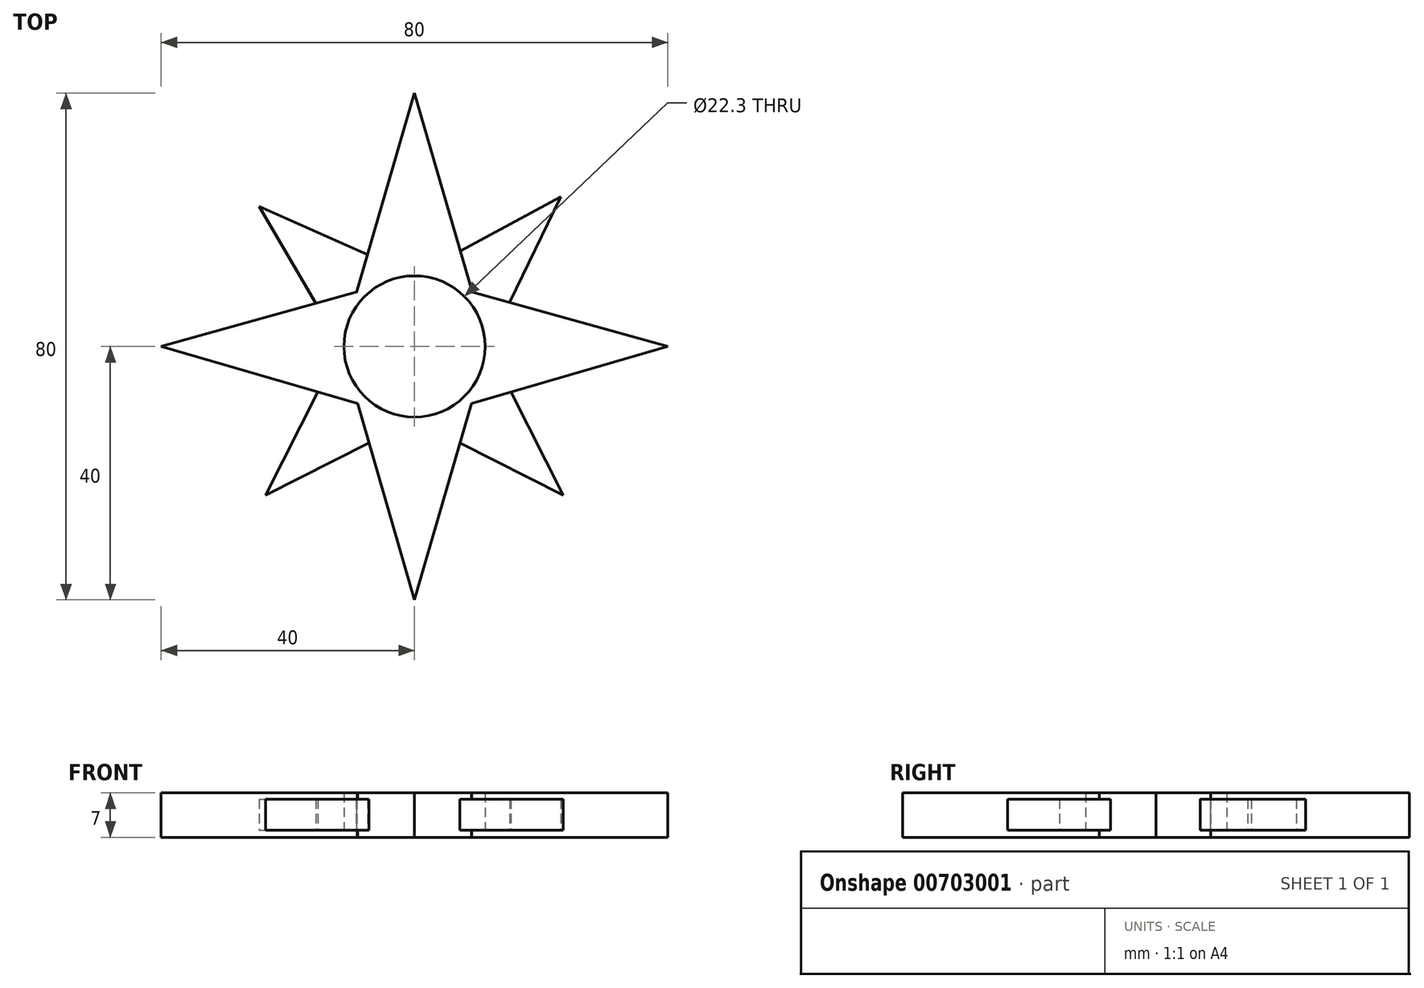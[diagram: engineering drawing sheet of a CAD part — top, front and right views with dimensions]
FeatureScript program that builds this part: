
annotation { "Feature Type Name" : "Feature", "Feature Type Description" : "" }
export const myFeature = defineFeature(function(context is Context, id is Id, definition is map)
    precondition{}
    {
        {
            var Q0;
            Q0=qCreatedBy(makeId("Top.planeOp"),FACE);
            var sketch = newSketch(context, id + "F0", { "sketchPlane" : qUnion([Q0])});
            skCircle(sketch, "E0", {"center": v(0, 0) * mm, "radius": 11.15 * mm});
            skLineSegment(sketch, "E1", {"start": v(0, 0) * mm, "end": v(0, 40) * mm});
            skLineSegment(sketch, "E2", {"start": v(0, 40) * mm, "end": v(-11.61, 0) * mm});
            skLineSegment(sketch, "E3", {"start": v(0, 40) * mm, "end": v(11.61, 0) * mm});
            skLineSegment(sketch, "E4", {"start": v(0, 0) * mm, "end": v(-40, 0) * mm});
            skLineSegment(sketch, "E5", {"start": v(0, 0) * mm, "end": v(0, -40) * mm});
            skLineSegment(sketch, "E6", {"start": v(0, 0) * mm, "end": v(40, 0) * mm});
            skLineSegment(sketch, "E7", {"start": v(0, 11.15) * mm, "end": v(-40, 0) * mm});
            skLineSegment(sketch, "E8", {"start": v(-40, 0) * mm, "end": v(0, -11.61) * mm});
            skLineSegment(sketch, "E9", {"start": v(0, -40) * mm, "end": v(-11.61, 0) * mm});
            skLineSegment(sketch, "E10", {"start": v(0, -40) * mm, "end": v(11.61, 0) * mm});
            skLineSegment(sketch, "E11", {"start": v(0, -11.61) * mm, "end": v(40, 0) * mm});
            skLineSegment(sketch, "E12", {"start": v(-11.61, 0) * mm, "end": v(0, 11.15) * mm});
            skLineSegment(sketch, "E13", {"start": v(0, 11.15) * mm, "end": v(40, 0) * mm});
            skLineSegment(sketch, "E14", {"start": v(-11.61, 0) * mm, "end": v(0, -11.61) * mm});
            skLineSegment(sketch, "E15", {"start": v(0, -11.61) * mm, "end": v(11.61, 0) * mm});
            skLineSegment(sketch, "E16", {"start": v(11.61, 0) * mm, "end": v(0, 11.15) * mm});
            skLineSegment(sketch, "E17", {"start": v(-5.8, 5.57) * mm, "end": v(-24.54, 22.13) * mm});
            skLineSegment(sketch, "E18", {"start": v(5.8, 5.58) * mm, "end": v(23.12, 23.6) * mm});
            skLineSegment(sketch, "E19", {"start": v(5.8, -5.8) * mm, "end": v(23.48, -23.48) * mm});
            skLineSegment(sketch, "E20", {"start": v(-5.8, -5.8) * mm, "end": v(-23.48, -23.48) * mm});
            skLineSegment(sketch, "E21", {"start": v(-24.54, 22.13) * mm, "end": v(-11.61, 0) * mm});
            skLineSegment(sketch, "E22", {"start": v(-24.54, 22.13) * mm, "end": v(0, 11.15) * mm});
            skLineSegment(sketch, "E23", {"start": v(0, 11.15) * mm, "end": v(23.12, 23.6) * mm});
            skLineSegment(sketch, "E24", {"start": v(23.12, 23.6) * mm, "end": v(11.61, 0) * mm});
            skLineSegment(sketch, "E25", {"start": v(11.61, 0) * mm, "end": v(23.48, -23.48) * mm});
            skLineSegment(sketch, "E26", {"start": v(23.48, -23.48) * mm, "end": v(0, -11.61) * mm});
            skLineSegment(sketch, "E27", {"start": v(0, -11.61) * mm, "end": v(-23.48, -23.48) * mm});
            skLineSegment(sketch, "E28", {"start": v(-23.48, -23.48) * mm, "end": v(-11.61, 0) * mm});
            skSolve(sketch);
        }
        {
            var Q0;
            {var subQ0=sQuery(id+"F0.wireOp",EDGE,"E2");var subQ3=sQuery(id+"F0.wireOp",EDGE,"E22");var subQ5=makeQuery(id+"F0.imprint","INTERSECT",VERTEX,{"derivedFrom":[subQ0,subQ3]});Q0=makeQuery(id+"F0.imprint","IMPRINT",FACE,{"disambiguationData":[TD([[makeQuery(id+"F0.imprint","IMPRINT",EDGE,{"disambiguationData":[TD([[subQ5,1.0]])],"derivedFrom":subQ0}),1.0]])]});}
            var Q1;
            {var subQ0=sQuery(id+"F0.wireOp",EDGE,"E3");var subQ3=sQuery(id+"F0.wireOp",EDGE,"E23");var subQ5=makeQuery(id+"F0.imprint","INTERSECT",VERTEX,{"derivedFrom":[subQ0,subQ3]});Q1=makeQuery(id+"F0.imprint","IMPRINT",FACE,{"disambiguationData":[TD([[makeQuery(id+"F0.imprint","IMPRINT",EDGE,{"disambiguationData":[TD([[subQ5,1.0]])],"derivedFrom":subQ0}),-1.0]])]});}
            var Q2;
            {var subQ0=sQuery(id+"F0.wireOp",EDGE,"E21");var subQ3=sQuery(id+"F0.wireOp",EDGE,"E7");var subQ5=makeQuery(id+"F0.imprint","INTERSECT",VERTEX,{"derivedFrom":[subQ3,subQ0]});Q2=makeQuery(id+"F0.imprint","IMPRINT",FACE,{"disambiguationData":[TD([[makeQuery(id+"F0.imprint","IMPRINT",EDGE,{"disambiguationData":[TD([[subQ5,-1.0]])],"derivedFrom":subQ3}),1.0]])]});}
            var Q3;
            {var subQ0=sQuery(id+"F0.wireOp",EDGE,"E28");var subQ3=sQuery(id+"F0.wireOp",EDGE,"E8");var subQ5=makeQuery(id+"F0.imprint","INTERSECT",VERTEX,{"derivedFrom":[subQ3,subQ0]});Q3=makeQuery(id+"F0.imprint","IMPRINT",FACE,{"disambiguationData":[TD([[makeQuery(id+"F0.imprint","IMPRINT",EDGE,{"disambiguationData":[TD([[subQ5,1.0]])],"derivedFrom":subQ3}),1.0]])]});}
            var Q4;
            {var subQ0=sQuery(id+"F0.wireOp",EDGE,"E9");var subQ3=sQuery(id+"F0.wireOp",EDGE,"E27");var subQ5=makeQuery(id+"F0.imprint","INTERSECT",VERTEX,{"derivedFrom":[subQ0,subQ3]});Q4=makeQuery(id+"F0.imprint","IMPRINT",FACE,{"disambiguationData":[TD([[makeQuery(id+"F0.imprint","IMPRINT",EDGE,{"disambiguationData":[TD([[subQ5,1.0]])],"derivedFrom":subQ0}),-1.0]])]});}
            var Q5;
            {var subQ0=sQuery(id+"F0.wireOp",EDGE,"E10");var subQ3=sQuery(id+"F0.wireOp",EDGE,"E26");var subQ5=makeQuery(id+"F0.imprint","INTERSECT",VERTEX,{"derivedFrom":[subQ0,subQ3]});Q5=makeQuery(id+"F0.imprint","IMPRINT",FACE,{"disambiguationData":[TD([[makeQuery(id+"F0.imprint","IMPRINT",EDGE,{"disambiguationData":[TD([[subQ5,1.0]])],"derivedFrom":subQ0}),1.0]])]});}
            var Q6;
            {var subQ0=sQuery(id+"F0.wireOp",EDGE,"E25");var subQ3=sQuery(id+"F0.wireOp",EDGE,"E11");var subQ5=makeQuery(id+"F0.imprint","INTERSECT",VERTEX,{"derivedFrom":[subQ3,subQ0]});Q6=makeQuery(id+"F0.imprint","IMPRINT",FACE,{"disambiguationData":[TD([[makeQuery(id+"F0.imprint","IMPRINT",EDGE,{"disambiguationData":[TD([[subQ5,-1.0]])],"derivedFrom":subQ3}),1.0]])]});}
            var Q7;
            {var subQ0=sQuery(id+"F0.wireOp",EDGE,"E24");var subQ3=sQuery(id+"F0.wireOp",EDGE,"E13");var subQ5=makeQuery(id+"F0.imprint","INTERSECT",VERTEX,{"derivedFrom":[subQ3,subQ0]});Q7=makeQuery(id+"F0.imprint","IMPRINT",FACE,{"disambiguationData":[TD([[makeQuery(id+"F0.imprint","IMPRINT",EDGE,{"disambiguationData":[TD([[subQ5,-1.0]])],"derivedFrom":subQ3}),-1.0]])]});}
            var Q8;
            {var subQ0=sQuery(id+"F0.wireOp",EDGE,"E22");var subQ5=sQuery(id+"F0.wireOp",EDGE,"E2");var subQ6=makeQuery(id+"F0.imprint","INTERSECT",VERTEX,{"derivedFrom":[subQ5,subQ0]});Q8=makeQuery(id+"F0.imprint","IMPRINT",FACE,{"disambiguationData":[TD([[makeQuery(id+"F0.imprint","IMPRINT",EDGE,{"disambiguationData":[TD([[subQ6,-1.0]])],"derivedFrom":subQ5}),1.0]])]});}
            var Q9;
            {var subQ0=sQuery(id+"F0.wireOp",EDGE,"E3");var subQ1=makeQuery(id+"F0.imprint","INTERSECT",VERTEX,{"derivedFrom":[sQuery(id+"F0.wireOp",EDGE,"E0"),subQ0]});Q9=makeQuery(id+"F0.imprint","IMPRINT",FACE,{"disambiguationData":[TD([[makeQuery(id+"F0.imprint","IMPRINT",EDGE,{"disambiguationData":[TD([[subQ1,1.0]])],"derivedFrom":subQ0}),1.0]])]});}
            var Q10;
            {var subQ0=sQuery(id+"F0.wireOp",EDGE,"E28");var subQ1=sQuery(id+"F0.wireOp",EDGE,"E8");var subQ2=makeQuery(id+"F0.imprint","INTERSECT",VERTEX,{"derivedFrom":[subQ1,subQ0]});Q10=makeQuery(id+"F0.imprint","IMPRINT",FACE,{"disambiguationData":[TD([[makeQuery(id+"F0.imprint","IMPRINT",EDGE,{"disambiguationData":[TD([[subQ2,-1.0]])],"derivedFrom":subQ1}),1.0]])]});}
            var Q11;
            {var subQ0=sQuery(id+"F0.wireOp",EDGE,"E8");var subQ1=makeQuery(id+"F0.imprint","INTERSECT",VERTEX,{"derivedFrom":[sQuery(id+"F0.wireOp",EDGE,"E0"),subQ0]});Q11=makeQuery(id+"F0.imprint","IMPRINT",FACE,{"disambiguationData":[TD([[makeQuery(id+"F0.imprint","IMPRINT",EDGE,{"disambiguationData":[TD([[subQ1,1.0]])],"derivedFrom":subQ0}),-1.0]])]});}
            var Q12;
            {var subQ0=sQuery(id+"F0.wireOp",EDGE,"E26");var subQ1=sQuery(id+"F0.wireOp",EDGE,"E10");var subQ2=makeQuery(id+"F0.imprint","INTERSECT",VERTEX,{"derivedFrom":[subQ1,subQ0]});Q12=makeQuery(id+"F0.imprint","IMPRINT",FACE,{"disambiguationData":[TD([[makeQuery(id+"F0.imprint","IMPRINT",EDGE,{"disambiguationData":[TD([[subQ2,-1.0]])],"derivedFrom":subQ1}),1.0]])]});}
            var Q13;
            {var subQ0=sQuery(id+"F0.wireOp",EDGE,"E10");var subQ1=makeQuery(id+"F0.imprint","INTERSECT",VERTEX,{"derivedFrom":[sQuery(id+"F0.wireOp",EDGE,"E0"),subQ0]});Q13=makeQuery(id+"F0.imprint","IMPRINT",FACE,{"disambiguationData":[TD([[makeQuery(id+"F0.imprint","IMPRINT",EDGE,{"disambiguationData":[TD([[subQ1,1.0]])],"derivedFrom":subQ0}),-1.0]])]});}
            var Q14;
            {var subQ5=sQuery(id+"F0.wireOp",EDGE,"E23");var subQ7=sQuery(id+"F0.wireOp",EDGE,"E3");var subQ8=makeQuery(id+"F0.imprint","INTERSECT",VERTEX,{"derivedFrom":[subQ7,subQ5]});Q14=makeQuery(id+"F0.imprint","IMPRINT",FACE,{"disambiguationData":[TD([[makeQuery(id+"F0.imprint","IMPRINT",EDGE,{"disambiguationData":[TD([[subQ8,-1.0]])],"derivedFrom":subQ7}),-1.0]])]});}
            var Q15;
            {var subQ1=sQuery(id+"F0.wireOp",EDGE,"E2");var subQ8=makeQuery(id+"F0.imprint","INTERSECT",VERTEX,{"derivedFrom":[sQuery(id+"F0.wireOp",EDGE,"E0"),subQ1]});Q15=makeQuery(id+"F0.imprint","IMPRINT",FACE,{"disambiguationData":[TD([[makeQuery(id+"F0.imprint","IMPRINT",EDGE,{"disambiguationData":[TD([[subQ8,1.0]])],"derivedFrom":subQ1}),-1.0]])]});}
            var Q16;
            {var subQ0=sQuery(id+"F0.wireOp",EDGE,"E17");var subQ1=sQuery(id+"F0.wireOp",EDGE,"E0");var subQ2=makeQuery(id+"F0.imprint","INTERSECT",VERTEX,{"derivedFrom":[subQ1,subQ0]});Q16=makeQuery(id+"F0.imprint","IMPRINT",FACE,{"disambiguationData":[TD([[makeQuery(id+"F0.imprint","IMPRINT",EDGE,{"disambiguationData":[TD([[subQ2,-1.0]])],"derivedFrom":subQ1}),-1.0]])]});}
            var Q17;
            {var subQ0=sQuery(id+"F0.wireOp",EDGE,"E18");var subQ1=sQuery(id+"F0.wireOp",EDGE,"E0");var subQ2=makeQuery(id+"F0.imprint","INTERSECT",VERTEX,{"derivedFrom":[subQ1,subQ0]});Q17=makeQuery(id+"F0.imprint","IMPRINT",FACE,{"disambiguationData":[TD([[makeQuery(id+"F0.imprint","IMPRINT",EDGE,{"disambiguationData":[TD([[subQ2,-1.0]])],"derivedFrom":subQ1}),-1.0]])]});}
            var Q18;
            {var subQ0=sQuery(id+"F0.wireOp",EDGE,"E7");var subQ1=sQuery(id+"F0.wireOp",EDGE,"E0");var subQ2=makeQuery(id+"F0.imprint","INTERSECT",VERTEX,{"derivedFrom":[subQ1,subQ0]});Q18=makeQuery(id+"F0.imprint","IMPRINT",FACE,{"disambiguationData":[TD([[makeQuery(id+"F0.imprint","IMPRINT",EDGE,{"disambiguationData":[TD([[subQ2,-1.0]])],"derivedFrom":subQ1}),-1.0]])]});}
            var Q19;
            {var subQ0=sQuery(id+"F0.wireOp",EDGE,"E3");var subQ1=sQuery(id+"F0.wireOp",EDGE,"E0");var subQ2=makeQuery(id+"F0.imprint","INTERSECT",VERTEX,{"derivedFrom":[subQ1,subQ0]});Q19=makeQuery(id+"F0.imprint","IMPRINT",FACE,{"disambiguationData":[TD([[makeQuery(id+"F0.imprint","IMPRINT",EDGE,{"disambiguationData":[TD([[subQ2,-1.0]])],"derivedFrom":subQ1}),-1.0]])]});}
            var Q20;
            {var subQ0=sQuery(id+"F0.wireOp",EDGE,"E11");var subQ1=sQuery(id+"F0.wireOp",EDGE,"E0");var subQ2=makeQuery(id+"F0.imprint","INTERSECT",VERTEX,{"derivedFrom":[subQ1,subQ0]});Q20=makeQuery(id+"F0.imprint","IMPRINT",FACE,{"disambiguationData":[TD([[makeQuery(id+"F0.imprint","IMPRINT",EDGE,{"disambiguationData":[TD([[subQ2,-1.0]])],"derivedFrom":subQ1}),-1.0]])]});}
            var Q21;
            {var subQ0=sQuery(id+"F0.wireOp",EDGE,"E19");var subQ1=sQuery(id+"F0.wireOp",EDGE,"E0");var subQ2=makeQuery(id+"F0.imprint","INTERSECT",VERTEX,{"derivedFrom":[subQ1,subQ0]});Q21=makeQuery(id+"F0.imprint","IMPRINT",FACE,{"disambiguationData":[TD([[makeQuery(id+"F0.imprint","IMPRINT",EDGE,{"disambiguationData":[TD([[subQ2,-1.0]])],"derivedFrom":subQ1}),-1.0]])]});}
            var Q22;
            {var subQ0=sQuery(id+"F0.wireOp",EDGE,"E20");var subQ1=sQuery(id+"F0.wireOp",EDGE,"E0");var subQ2=makeQuery(id+"F0.imprint","INTERSECT",VERTEX,{"derivedFrom":[subQ1,subQ0]});Q22=makeQuery(id+"F0.imprint","IMPRINT",FACE,{"disambiguationData":[TD([[makeQuery(id+"F0.imprint","IMPRINT",EDGE,{"disambiguationData":[TD([[subQ2,-1.0]])],"derivedFrom":subQ1}),-1.0]])]});}
            var Q23;
            {var subQ0=sQuery(id+"F0.wireOp",EDGE,"E9");var subQ1=sQuery(id+"F0.wireOp",EDGE,"E0");var subQ2=makeQuery(id+"F0.imprint","INTERSECT",VERTEX,{"derivedFrom":[subQ1,subQ0]});Q23=makeQuery(id+"F0.imprint","IMPRINT",FACE,{"disambiguationData":[TD([[makeQuery(id+"F0.imprint","IMPRINT",EDGE,{"disambiguationData":[TD([[subQ2,-1.0]])],"derivedFrom":subQ1}),-1.0]])]});}
            var Q24;
            {var subQ0=sQuery(id+"F0.wireOp",EDGE,"E14");var subQ1=sQuery(id+"F0.wireOp",EDGE,"E0");var subQ2=makeQuery(id+"F0.imprint","INTERSECT",VERTEX,{"disambiguationData":[OD(0.0)],"derivedFrom":[subQ1,subQ0]});Q24=makeQuery(id+"F0.imprint","IMPRINT",FACE,{"disambiguationData":[TD([[makeQuery(id+"F0.imprint","IMPRINT",EDGE,{"disambiguationData":[TD([[subQ2,-1.0]])],"derivedFrom":subQ1}),-1.0]])]});}
            var Q25;
            {var subQ0=sQuery(id+"F0.wireOp",EDGE,"E4");var subQ1=sQuery(id+"F0.wireOp",EDGE,"E0");var subQ2=makeQuery(id+"F0.imprint","INTERSECT",VERTEX,{"derivedFrom":[subQ1,subQ0]});Q25=makeQuery(id+"F0.imprint","IMPRINT",FACE,{"disambiguationData":[TD([[makeQuery(id+"F0.imprint","IMPRINT",EDGE,{"disambiguationData":[TD([[subQ2,-1.0]])],"derivedFrom":subQ1}),-1.0]])]});}
            var Q26;
            {var subQ0=sQuery(id+"F0.wireOp",EDGE,"E12");var subQ1=sQuery(id+"F0.wireOp",EDGE,"E0");var subQ2=makeQuery(id+"F0.imprint","INTERSECT",VERTEX,{"derivedFrom":[subQ1,subQ0]});Q26=makeQuery(id+"F0.imprint","IMPRINT",FACE,{"disambiguationData":[TD([[makeQuery(id+"F0.imprint","IMPRINT",EDGE,{"disambiguationData":[TD([[subQ2,-1.0]])],"derivedFrom":subQ1}),-1.0]])]});}
            var Q27;
            {var subQ0=sQuery(id+"F0.wireOp",EDGE,"E2");var subQ1=sQuery(id+"F0.wireOp",EDGE,"E0");var subQ2=makeQuery(id+"F0.imprint","INTERSECT",VERTEX,{"derivedFrom":[subQ1,subQ0]});Q27=makeQuery(id+"F0.imprint","IMPRINT",FACE,{"disambiguationData":[TD([[makeQuery(id+"F0.imprint","IMPRINT",EDGE,{"disambiguationData":[TD([[subQ2,-1.0]])],"derivedFrom":subQ1}),-1.0]])]});}
            var Q28;
            {var subQ0=sQuery(id+"F0.wireOp",EDGE,"E10");var subQ1=sQuery(id+"F0.wireOp",EDGE,"E0");var subQ2=makeQuery(id+"F0.imprint","INTERSECT",VERTEX,{"derivedFrom":[subQ1,subQ0]});Q28=makeQuery(id+"F0.imprint","IMPRINT",FACE,{"disambiguationData":[TD([[makeQuery(id+"F0.imprint","IMPRINT",EDGE,{"disambiguationData":[TD([[subQ2,-1.0]])],"derivedFrom":subQ1}),-1.0]])]});}
            var Q29;
            {var subQ0=sQuery(id+"F0.wireOp",EDGE,"E6");var subQ1=sQuery(id+"F0.wireOp",EDGE,"E0");var subQ2=makeQuery(id+"F0.imprint","INTERSECT",VERTEX,{"derivedFrom":[subQ1,subQ0]});Q29=makeQuery(id+"F0.imprint","IMPRINT",FACE,{"disambiguationData":[TD([[makeQuery(id+"F0.imprint","IMPRINT",EDGE,{"disambiguationData":[TD([[subQ2,1.0]])],"derivedFrom":subQ1}),-1.0]])]});}
            var Q30;
            {var subQ0=sQuery(id+"F0.wireOp",EDGE,"E16");var subQ1=sQuery(id+"F0.wireOp",EDGE,"E0");var subQ2=makeQuery(id+"F0.imprint","INTERSECT",VERTEX,{"derivedFrom":[subQ1,subQ0]});Q30=makeQuery(id+"F0.imprint","IMPRINT",FACE,{"disambiguationData":[TD([[makeQuery(id+"F0.imprint","IMPRINT",EDGE,{"disambiguationData":[TD([[subQ2,1.0]])],"derivedFrom":subQ1}),-1.0]])]});}
            var Q31;
            {var subQ0=sQuery(id+"F0.wireOp",EDGE,"E16");var subQ1=sQuery(id+"F0.wireOp",EDGE,"E0");var subQ2=makeQuery(id+"F0.imprint","INTERSECT",VERTEX,{"derivedFrom":[subQ1,subQ0]});Q31=makeQuery(id+"F0.imprint","IMPRINT",FACE,{"disambiguationData":[TD([[makeQuery(id+"F0.imprint","IMPRINT",EDGE,{"disambiguationData":[TD([[subQ2,-1.0]])],"derivedFrom":subQ1}),-1.0]])]});}
            var Q32;
            {var subQ0=sQuery(id+"F0.wireOp",EDGE,"E18");var subQ1=sQuery(id+"F0.wireOp",EDGE,"E3");var subQ2=makeQuery(id+"F0.imprint","INTERSECT",VERTEX,{"derivedFrom":[subQ1,subQ0]});Q32=makeQuery(id+"F0.imprint","IMPRINT",FACE,{"disambiguationData":[TD([[makeQuery(id+"F0.imprint","IMPRINT",EDGE,{"disambiguationData":[TD([[subQ2,-1.0]])],"derivedFrom":subQ1}),-1.0]])]});}
            var Q33;
            {var subQ0=sQuery(id+"F0.wireOp",EDGE,"E8");var subQ1=sQuery(id+"F0.wireOp",EDGE,"E0");var subQ2=makeQuery(id+"F0.imprint","INTERSECT",VERTEX,{"derivedFrom":[subQ1,subQ0]});Q33=makeQuery(id+"F0.imprint","IMPRINT",FACE,{"disambiguationData":[TD([[makeQuery(id+"F0.imprint","IMPRINT",EDGE,{"disambiguationData":[TD([[subQ2,-1.0]])],"derivedFrom":subQ1}),-1.0]])]});}
            var Q34;
            {var subQ0=sQuery(id+"F0.wireOp",EDGE,"E5");var subQ1=sQuery(id+"F0.wireOp",EDGE,"E0");var subQ2=makeQuery(id+"F0.imprint","INTERSECT",VERTEX,{"derivedFrom":[subQ1,subQ0]});Q34=makeQuery(id+"F0.imprint","IMPRINT",FACE,{"disambiguationData":[TD([[makeQuery(id+"F0.imprint","IMPRINT",EDGE,{"disambiguationData":[TD([[subQ2,-1.0]])],"derivedFrom":subQ1}),-1.0]])]});}
            var Q35;
            {var subQ0=sQuery(id+"F0.wireOp",EDGE,"E15");var subQ1=sQuery(id+"F0.wireOp",EDGE,"E0");var subQ2=makeQuery(id+"F0.imprint","INTERSECT",VERTEX,{"disambiguationData":[OD(0.0)],"derivedFrom":[subQ1,subQ0]});Q35=makeQuery(id+"F0.imprint","IMPRINT",FACE,{"disambiguationData":[TD([[makeQuery(id+"F0.imprint","IMPRINT",EDGE,{"disambiguationData":[TD([[subQ2,-1.0]])],"derivedFrom":subQ1}),-1.0]])]});}
            var Q36;
            {var subQ0=sQuery(id+"F0.wireOp",EDGE,"E14");var subQ1=sQuery(id+"F0.wireOp",EDGE,"E0");var subQ2=makeQuery(id+"F0.imprint","INTERSECT",VERTEX,{"disambiguationData":[OD(1.0)],"derivedFrom":[subQ1,subQ0]});Q36=makeQuery(id+"F0.imprint","IMPRINT",FACE,{"disambiguationData":[TD([[makeQuery(id+"F0.imprint","IMPRINT",EDGE,{"disambiguationData":[TD([[subQ2,-1.0]])],"derivedFrom":subQ1}),-1.0]])]});}
            extrude(context, id + "F1", {"entities" : qUnion([Q0, Q1, Q2, Q3, Q4, Q5, Q6, Q7, Q8, Q9, Q10, Q11, Q12, Q13, Q14, Q15, Q16, Q17, Q18, Q19, Q20, Q21, Q22, Q23, Q24, Q25, Q26, Q27, Q28, Q29, Q30, Q31, Q32, Q33, Q34, Q35, Q36]), "depth" : 7 * mm, "offsetDistance" : 25 * mm});
        }
        {
            var Q0;
            {var subQ0=sQuery(id+"F0.wireOp",EDGE,"E21");var subQ1=sQuery(id+"F0.wireOp",EDGE,"E7");var subQ2=makeQuery(id+"F0.imprint","INTERSECT",VERTEX,{"derivedFrom":[subQ1,subQ0]});Q0=makeQuery(id+"F0.imprint","IMPRINT",FACE,{"disambiguationData":[TD([[makeQuery(id+"F0.imprint","IMPRINT",EDGE,{"disambiguationData":[TD([[subQ2,1.0]])],"derivedFrom":subQ1}),-1.0]])]});}
            var Q1;
            {var subQ0=sQuery(id+"F0.wireOp",EDGE,"E22");var subQ1=sQuery(id+"F0.wireOp",EDGE,"E2");var subQ2=makeQuery(id+"F0.imprint","INTERSECT",VERTEX,{"derivedFrom":[subQ1,subQ0]});Q1=makeQuery(id+"F0.imprint","IMPRINT",FACE,{"disambiguationData":[TD([[makeQuery(id+"F0.imprint","IMPRINT",EDGE,{"disambiguationData":[TD([[subQ2,-1.0]])],"derivedFrom":subQ1}),-1.0]])]});}
            var Q2;
            {var subQ0=sQuery(id+"F0.wireOp",EDGE,"E23");var subQ1=sQuery(id+"F0.wireOp",EDGE,"E3");var subQ2=makeQuery(id+"F0.imprint","INTERSECT",VERTEX,{"derivedFrom":[subQ1,subQ0]});Q2=makeQuery(id+"F0.imprint","IMPRINT",FACE,{"disambiguationData":[TD([[makeQuery(id+"F0.imprint","IMPRINT",EDGE,{"disambiguationData":[TD([[subQ2,-1.0]])],"derivedFrom":subQ1}),1.0]])]});}
            var Q3;
            {var subQ0=sQuery(id+"F0.wireOp",EDGE,"E18");var subQ1=sQuery(id+"F0.wireOp",EDGE,"E3");var subQ2=makeQuery(id+"F0.imprint","INTERSECT",VERTEX,{"derivedFrom":[subQ1,subQ0]});Q3=makeQuery(id+"F0.imprint","IMPRINT",FACE,{"disambiguationData":[TD([[makeQuery(id+"F0.imprint","IMPRINT",EDGE,{"disambiguationData":[TD([[subQ2,-1.0]])],"derivedFrom":subQ1}),1.0]])]});}
            var Q4;
            {var subQ0=sQuery(id+"F0.wireOp",EDGE,"E25");var subQ1=sQuery(id+"F0.wireOp",EDGE,"E11");var subQ2=makeQuery(id+"F0.imprint","INTERSECT",VERTEX,{"derivedFrom":[subQ1,subQ0]});Q4=makeQuery(id+"F0.imprint","IMPRINT",FACE,{"disambiguationData":[TD([[makeQuery(id+"F0.imprint","IMPRINT",EDGE,{"disambiguationData":[TD([[subQ2,1.0]])],"derivedFrom":subQ1}),-1.0]])]});}
            var Q5;
            {var subQ0=sQuery(id+"F0.wireOp",EDGE,"E26");var subQ1=sQuery(id+"F0.wireOp",EDGE,"E10");var subQ2=makeQuery(id+"F0.imprint","INTERSECT",VERTEX,{"derivedFrom":[subQ1,subQ0]});Q5=makeQuery(id+"F0.imprint","IMPRINT",FACE,{"disambiguationData":[TD([[makeQuery(id+"F0.imprint","IMPRINT",EDGE,{"disambiguationData":[TD([[subQ2,-1.0]])],"derivedFrom":subQ1}),-1.0]])]});}
            var Q6;
            {var subQ0=sQuery(id+"F0.wireOp",EDGE,"E27");var subQ1=sQuery(id+"F0.wireOp",EDGE,"E9");var subQ2=makeQuery(id+"F0.imprint","INTERSECT",VERTEX,{"derivedFrom":[subQ1,subQ0]});Q6=makeQuery(id+"F0.imprint","IMPRINT",FACE,{"disambiguationData":[TD([[makeQuery(id+"F0.imprint","IMPRINT",EDGE,{"disambiguationData":[TD([[subQ2,-1.0]])],"derivedFrom":subQ1}),1.0]])]});}
            var Q7;
            {var subQ0=sQuery(id+"F0.wireOp",EDGE,"E28");var subQ1=sQuery(id+"F0.wireOp",EDGE,"E8");var subQ2=makeQuery(id+"F0.imprint","INTERSECT",VERTEX,{"derivedFrom":[subQ1,subQ0]});Q7=makeQuery(id+"F0.imprint","IMPRINT",FACE,{"disambiguationData":[TD([[makeQuery(id+"F0.imprint","IMPRINT",EDGE,{"disambiguationData":[TD([[subQ2,-1.0]])],"derivedFrom":subQ1}),-1.0]])]});}
            extrude(context, id + "F2", {"entities" : qUnion([Q0, Q1, Q2, Q3, Q4, Q5, Q6, Q7]), "operationType" : NewBodyOperationType.ADD, "depth" : 6 * mm, "offsetDistance" : 25 * mm, "hasSecondDirection" : true, "secondDirectionOppositeDirection" : false, "secondDirectionDepth" : 1.1 * mm});
        }
    });
